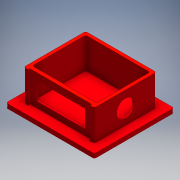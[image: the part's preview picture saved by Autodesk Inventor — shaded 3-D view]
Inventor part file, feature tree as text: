
AUTODESK INVENTOR PART (.ipt)
format: ipt  version: 2016 (Build 200138000, 138)  size: 264,192 bytes
history: native  units: mm
features: extrude x9, sketch x9
ambient origin geometry x8: Origin, YZ Plane, XZ Plane, XY Plane, X Axis, Y Axis, Z Axis, Center Point
bodies: Solid1 (feature_tree)
feature tree (18):
  extrude  "base"  Depth=70.0mm
  extrude  "walls"  Depth=40.0mm
  extrude  "magnets"  Depth=5.0mm TaperAngle=0.0deg
  extrude  "xyStageMount"  Depth=3.5mm
  extrude  "coverSlipWindowExt"  Depth=3.5mm
  extrude  "rectWindowExt"  Depth=35.0mm TaperAngle=0.0deg
  extrude  "objWindowExt"  Depth=15.0mm
  extrude  "coverSlipWindowCirc"  Depth=15.0mm
  extrude  "coverSlipCircExt"  Depth=27.0mm
  sketch  "Sketch1"  dims[d0=80.0mm d1=70.0mm]
  sketch  "Sketch2"  dims[d2=35.0mm d3=40.0mm]
  sketch  "Sketch7"  dims[d4=2.0mm d5=5.0mm d6=0.0mm]
  sketch  "Sketch10"  dims[d7=2.0mm d8=3.5mm]
  sketch  "Sketch15"  dims[d9=3.5mm d10=3.5mm]
  sketch  "Sketch16"  dims[d12=2.0mm d13=35.0mm d14=0.0mm]
  sketch  "Sketch17"  dims[d40=15.0mm d41=15.0mm]
  sketch  "Sketch18"  dims[d42=15.0mm d51=15.0mm]
  sketch  "Sketch19"  dims[d52=15.0mm d53=5.75mm d54=5.75mm d55=5.75mm d56=5.75mm d57=5.75mm d58=2.5mm d59=0.0mm d73=10.0mm d74=10.0mm d75=10.0mm d76=10.0mm d77=2.0mm d78=5.0mm d79=0.0mm d107=20.0mm d108=55.0mm d109=27.5mm d111=5.0mm d112=5.0mm d113=5.0mm d114=5.0mm d115=2.0mm d116=0.0mm d117=2.0mm d118=0.0mm d120=70.0mm d121=35.0mm d123=6.0mm d124=2.0mm d125=0.0mm d128=30.0mm d129=17.0mm d130=2.0mm d131=0.0mm d133=19.5mm d134=2.0mm d135=0.0mm d136=27.0mm]
